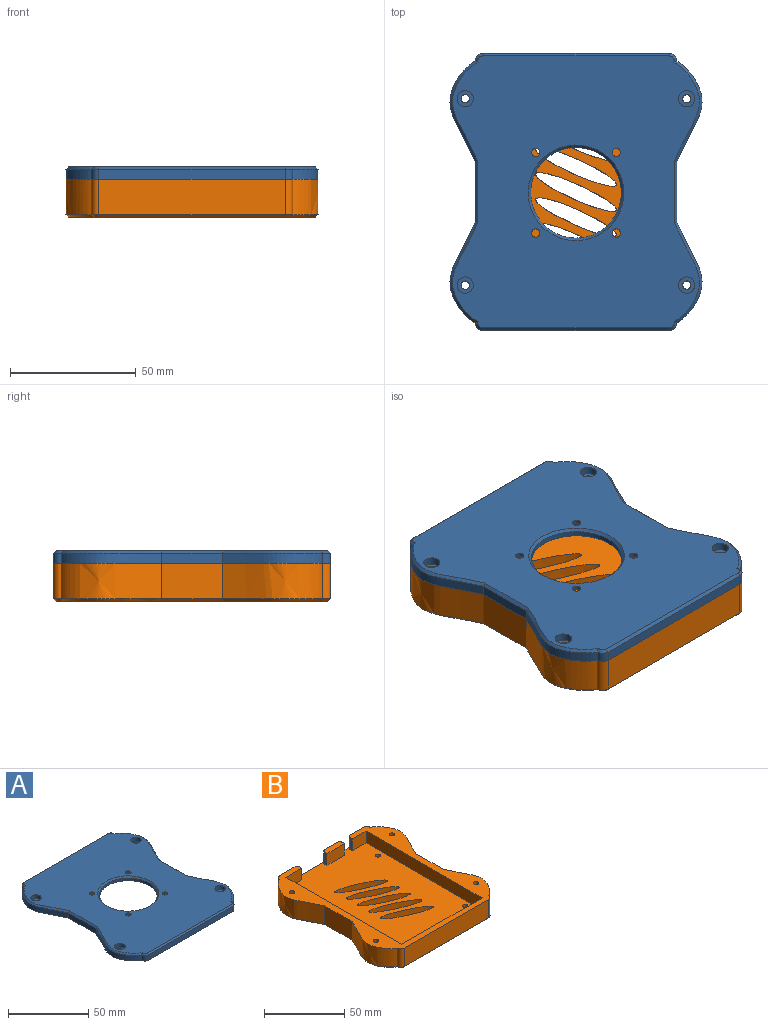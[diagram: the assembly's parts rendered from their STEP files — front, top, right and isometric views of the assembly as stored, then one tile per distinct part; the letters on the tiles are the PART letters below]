
ASSEMBLY  parts=2 mates=1
PART A: 53 faces, bbox 102.5x111.1x6.1 mm
  f0: plane 70.5x2mm, normal (0,1,0), area 141mm2, adj f1,f15,f16,f30
  f1: plane 102x2mm, normal (1,0,0), area 204mm2, adj f0,f2,f16,f30
  f2: plane 70.5x2mm, normal (0,-1,0), area 141mm2, adj f1,f15,f16,f30
  f3: extruded ~40x10.04mm, area 183.4mm2, adj f4,f14,f16,f51
  f4: plane 24x4mm, normal (-1,0,0), area 96mm2, adj f3,f5,f16,f49
  f5: extruded ~40x10.04mm, area 183.4mm2, adj f4,f6,f16,f47
  f6: cylinder r=3mm len=4mm, axis (0,0,1), area 18.8mm2, adj f5,f7,f16,f45
  f7: plane 74x4mm, normal (0,-1,0), area 296mm2, adj f6,f8,f16,f43
  f8: cylinder r=3mm len=4mm, axis (0,0,1), area 18.8mm2, adj f7,f9,f16,f41
  f9: extruded ~40x10.04mm, area 183.4mm2, adj f8,f10,f16,f42
  f10: plane 24x4mm, normal (1,0,0), area 96mm2, adj f9,f11,f16,f44
  f11: extruded ~40x10.04mm, area 183.4mm2, adj f10,f12,f16,f46
  f12: cylinder r=3mm len=4mm, axis (0,0,1), area 18.8mm2, adj f11,f13,f16,f48
  f13: plane 74x4mm, normal (0,1,0), area 296mm2, adj f12,f14,f16,f50
  f14: cylinder r=3mm len=4mm, axis (0,0,1), area 18.8mm2, adj f3,f13,f16,f52
  f15: plane 102x2mm, normal (-1,0,0), area 204mm2, adj f0,f2,f16,f30
  f16: plane 110x101.38mm, normal (0,0,-1), area 2552.6mm2, adj f0,f1,f2,f3,f4,f5,f6,f7
  f17: plane 109.12x99.61mm, normal (0,0,1), area 8092.7mm2, adj f20,f23,f26,f29,f31,f33,f35,f37
  f18: cylinder r=1.65mm len=3.3mm, axis (0,0,1), area 20.7mm2, adj f16,f19
  f19: plane 6.5x6.5mm, normal (0,0,1), area 24.6mm2, adj f18,f20
  f20: cylinder r=3.25mm len=6.5mm, axis (0,0,1), area 61.3mm2, adj f17,f19
  f21: cylinder r=1.65mm len=3.3mm, axis (0,0,1), area 20.7mm2, adj f16,f22
  f22: plane 6.5x6.5mm, normal (0,0,1), area 24.6mm2, adj f21,f23
  f23: cylinder r=3.25mm len=6.5mm, axis (0,0,1), area 61.3mm2, adj f17,f22
  f24: cylinder r=1.65mm len=3.3mm, axis (0,0,1), area 20.7mm2, adj f16,f25
  f25: plane 6.5x6.5mm, normal (0,0,1), area 24.6mm2, adj f24,f26
  f26: cylinder r=3.25mm len=6.5mm, axis (0,0,1), area 61.3mm2, adj f17,f25
  f27: cylinder r=1.65mm len=3.3mm, axis (0,0,1), area 20.7mm2, adj f16,f28
  f28: plane 6.5x6.5mm, normal (0,0,1), area 24.6mm2, adj f27,f29
  f29: cylinder r=3.25mm len=6.5mm, axis (0,0,1), area 61.3mm2, adj f17,f28
  f30: plane 102x70.5mm, normal (0,0,-1), area 6031.3mm2, adj f0,f1,f2,f15,f32,f34,f36,f38
  f31: cylinder r=1.65mm len=3.3mm, axis (0,0,-1), area 13.4mm2, adj f17,f32
  f32: cone r=1.65mm half-angle=45deg, axis (0,0,-1), area 38.1mm2, adj f30,f31
  f33: cylinder r=1.65mm len=3.3mm, axis (0,0,-1), area 13.4mm2, adj f17,f34
  f34: cone r=1.65mm half-angle=45deg, axis (0,0,-1), area 38.1mm2, adj f30,f33
  f35: cylinder r=1.65mm len=3.3mm, axis (0,0,-1), area 13.4mm2, adj f17,f36
  f36: cone r=1.65mm half-angle=45deg, axis (0,0,-1), area 38.1mm2, adj f30,f35
  f37: cylinder r=1.65mm len=3.3mm, axis (0,0,-1), area 13.4mm2, adj f17,f38
  f38: cone r=1.65mm half-angle=45deg, axis (0,0,-1), area 38.1mm2, adj f30,f37
  f39: cylinder r=18mm len=36mm, axis (0,0,-1), area 226.2mm2, adj f30,f40
  f40: cone r=18mm half-angle=45deg, axis (0,0,1), area 164.4mm2, adj f17,f39
  f41: cone r=2mm half-angle=45deg, axis (0,0,-1), area 6mm2, adj f8,f17,f42,f43
  f42: bspline ~40.52x11.13mm, area 64.4mm2, adj f9,f17,f41,f44
  f43: plane 74x1mm, normal (0,-0.71,0.71), area 104.7mm2, adj f7,f17,f41,f45
  f44: plane 24.39x1mm, normal (0.71,0,0.71), area 34.2mm2, adj f10,f17,f42,f46
  f45: cone r=2mm half-angle=45deg, axis (0,0,-1), area 6mm2, adj f6,f17,f43,f47
  f46: bspline ~43.19x12.21mm, area 64.4mm2, adj f11,f17,f44,f48
  f47: bspline ~43.19x12.21mm, area 64.4mm2, adj f5,f17,f45,f49
  f48: cone r=2mm half-angle=45deg, axis (0,0,-1), area 6mm2, adj f12,f17,f46,f50
  f49: plane 24.39x1mm, normal (-0.71,0,0.71), area 34.2mm2, adj f4,f17,f47,f51
  f50: plane 74x1mm, normal (0,0.71,0.71), area 104.7mm2, adj f13,f17,f48,f52
  f51: bspline ~40.52x11.13mm, area 64.4mm2, adj f3,f17,f49,f52
  f52: cone r=2mm half-angle=45deg, axis (0,0,-1), area 6mm2, adj f14,f17,f50,f51
PART B: 96 faces, bbox 102.5x111.1x16.1 mm
  f0: plane 15.5x9mm, normal (0,-1,0), area 139.5mm2, adj f2,f21,f67,f68
  f1: plane 12x9mm, normal (0,-1,0), area 108mm2, adj f3,f8,f21,f66
  f2: plane 15.5x4mm, normal (0,0,1), area 60.3mm2, adj f0,f4,f67,f68,f71,f73
  f3: plane 110x101.38mm, normal (0,0,1), area 2372.9mm2, adj f1,f4,f6,f7,f8,f9,f10,f11
  f4: plane 74x14mm, normal (0,1,0), area 703mm2, adj f2,f3,f12,f13,f21,f70,f71,f72
  f5: plane 109.12x99.61mm, normal (0,0,-1), area 7932mm2, adj f24,f27,f30,f33,f38,f39,f40,f41
  f6: plane 102x9mm, normal (1,0,0), area 918mm2, adj f3,f7,f9,f21
  f7: plane 70.5x9mm, normal (0,1,0), area 634.5mm2, adj f3,f6,f8,f21
  f8: plane 102x9mm, normal (-1,0,0), area 918mm2, adj f1,f3,f7,f21
  f9: plane 14x9mm, normal (0,-1,0), area 126mm2, adj f3,f6,f21,f69
  f10: plane 24x14mm, normal (1,0,0), area 336mm2, adj f3,f11,f20,f83
  f11: extruded ~40x14mm, area 641.9mm2, adj f3,f10,f12,f81
  f12: cylinder r=3mm len=14mm, axis (0,0,-1), area 66mm2, adj f3,f4,f11,f79
  f13: cylinder r=3mm len=14mm, axis (0,0,-1), area 66mm2, adj f3,f4,f14,f82
  f14: extruded ~40x14mm, area 641.9mm2, adj f3,f13,f15,f84
  f15: plane 24x14mm, normal (-1,0,0), area 336mm2, adj f3,f14,f16,f86
  f16: extruded ~40x14mm, area 641.9mm2, adj f3,f15,f17,f88
  f17: cylinder r=3mm len=14mm, axis (0,0,-1), area 66mm2, adj f3,f16,f18,f90
  f18: plane 74x14mm, normal (0,-1,0), area 1036mm2, adj f3,f17,f19,f89
  f19: cylinder r=3mm len=14mm, axis (0,0,-1), area 66mm2, adj f3,f18,f20,f87
  f20: extruded ~40x14mm, area 641.9mm2, adj f3,f10,f19,f85
  f21: plane 106x70.5mm, normal (0,0,1), area 6451.6mm2, adj f0,f1,f4,f6,f7,f8,f9,f22
  f22: cylinder r=1.65mm len=3.3mm, axis (0,0,-1), area 31.1mm2, adj f21,f23
  f23: plane 6.5x6.5mm, normal (0,0,-1), area 24.6mm2, adj f22,f24
  f24: cylinder r=3.25mm len=6.5mm, axis (0,0,-1), area 61.3mm2, adj f5,f23
  f25: cylinder r=1.65mm len=3.3mm, axis (0,0,-1), area 31.1mm2, adj f21,f26
  f26: plane 6.5x6.5mm, normal (0,0,-1), area 24.6mm2, adj f25,f27
  f27: cylinder r=3.25mm len=6.5mm, axis (0,0,-1), area 61.3mm2, adj f5,f26
  f28: cylinder r=1.65mm len=3.3mm, axis (0,0,-1), area 31.1mm2, adj f21,f29
  f29: plane 6.5x6.5mm, normal (0,0,-1), area 24.6mm2, adj f28,f30
  f30: cylinder r=3.25mm len=6.5mm, axis (0,0,-1), area 61.3mm2, adj f5,f29
  f31: cylinder r=1.65mm len=3.3mm, axis (0,0,-1), area 31.1mm2, adj f21,f32
  f32: plane 6.5x6.5mm, normal (0,0,-1), area 24.6mm2, adj f31,f33
  f33: cylinder r=3.25mm len=6.5mm, axis (0,0,-1), area 61.3mm2, adj f5,f32
  f34: cylinder r=1.65mm len=13mm, axis (0,0,-1), area 134.8mm2, adj f3,f65
  f35: cylinder r=1.65mm len=13mm, axis (0,0,-1), area 134.8mm2, adj f3,f58
  f36: cylinder r=1.65mm len=13mm, axis (0,0,-1), area 134.8mm2, adj f3,f51
  f37: cylinder r=1.65mm len=13mm, axis (0,0,-1), area 134.8mm2, adj f3,f44
  f38: plane 3.46x2mm, normal (-1,0,0), area 6.9mm2, adj f5,f39,f43,f44
  f39: plane 3x2mm, normal (-0.5,-0.87,0), area 6.9mm2, adj f5,f38,f40,f44
  f40: plane 3x2mm, normal (0.5,-0.87,0), area 6.9mm2, adj f5,f39,f41,f44
  f41: plane 3.46x2mm, normal (1,0,0), area 6.9mm2, adj f5,f40,f42,f44
  f42: plane 3x2mm, normal (0.5,0.87,0), area 6.9mm2, adj f5,f41,f43,f44
  f43: plane 3x2mm, normal (-0.5,0.87,0), area 6.9mm2, adj f5,f38,f42,f44
  f44: plane 6.93x6mm, normal (0,0,-1), area 22.6mm2, adj f37,f38,f39,f40,f41,f42,f43
  f45: plane 3x2mm, normal (-0.5,-0.87,0), area 6.9mm2, adj f5,f46,f50,f51
  f46: plane 3x2mm, normal (0.5,-0.87,0), area 6.9mm2, adj f5,f45,f47,f51
  f47: plane 3.46x2mm, normal (1,0,0), area 6.9mm2, adj f5,f46,f48,f51
  f48: plane 3x2mm, normal (0.5,0.87,0), area 6.9mm2, adj f5,f47,f49,f51
  f49: plane 3x2mm, normal (-0.5,0.87,0), area 6.9mm2, adj f5,f48,f50,f51
  f50: plane 3.46x2mm, normal (-1,0,0), area 6.9mm2, adj f5,f45,f49,f51
  f51: plane 6.93x6mm, normal (0,0,-1), area 22.6mm2, adj f36,f45,f46,f47,f48,f49,f50
  f52: plane 3.46x2mm, normal (-1,0,0), area 6.9mm2, adj f5,f53,f57,f58
  f53: plane 3x2mm, normal (-0.5,-0.87,0), area 6.9mm2, adj f5,f52,f54,f58
  f54: plane 3x2mm, normal (0.5,-0.87,0), area 6.9mm2, adj f5,f53,f55,f58
  f55: plane 3.46x2mm, normal (1,0,0), area 6.9mm2, adj f5,f54,f56,f58
  f56: plane 3x2mm, normal (0.5,0.87,0), area 6.9mm2, adj f5,f55,f57,f58
  f57: plane 3x2mm, normal (-0.5,0.87,0), area 6.9mm2, adj f5,f52,f56,f58
  f58: plane 6.93x6mm, normal (0,0,-1), area 22.6mm2, adj f35,f52,f53,f54,f55,f56,f57
  f59: plane 3x2mm, normal (0.5,0.87,0), area 6.9mm2, adj f5,f60,f64,f65
  f60: plane 3x2mm, normal (-0.5,0.87,0), area 6.9mm2, adj f5,f59,f61,f65
  f61: plane 3.46x2mm, normal (-1,0,0), area 6.9mm2, adj f5,f60,f62,f65
  f62: plane 3x2mm, normal (-0.5,-0.87,0), area 6.9mm2, adj f5,f61,f63,f65
  f63: plane 3x2mm, normal (0.5,-0.87,0), area 6.9mm2, adj f5,f62,f64,f65
  f64: plane 3.46x2mm, normal (1,0,0), area 6.9mm2, adj f5,f59,f63,f65
  f65: plane 6.93x6mm, normal (0,0,-1), area 22.6mm2, adj f34,f59,f60,f61,f62,f63,f64
  f66: plane 9x2mm, normal (-1,0,0), area 18mm2, adj f1,f3,f21,f70
  f67: plane 9x2mm, normal (1,0,0), area 18mm2, adj f0,f2,f21,f71
  f68: plane 9x2mm, normal (-1,0,0), area 18mm2, adj f0,f2,f21,f73
  f69: plane 9x2mm, normal (1,0,0), area 18mm2, adj f3,f9,f21,f72
  f70: cylinder r=2mm len=9mm, axis (0,0,1), area 28.3mm2, adj f3,f4,f21,f66
  f71: cylinder r=2mm len=9mm, axis (0,0,-1), area 28.3mm2, adj f2,f4,f21,f67
  f72: cylinder r=2mm len=9mm, axis (0,0,-1), area 28.3mm2, adj f3,f4,f21,f69
  f73: cylinder r=2mm len=9mm, axis (0,0,1), area 28.3mm2, adj f2,f4,f21,f68
  f74: extruded ~31.9x15.39mm, area 364.4mm2, adj f21,f95
  f75: extruded ~31.9x15.39mm, area 364.4mm2, adj f21,f92
  f76: extruded ~31.9x15.39mm, area 364.4mm2, adj f21,f91
  f77: extruded ~31.9x15.39mm, area 364.4mm2, adj f21,f94
  f78: extruded ~31.9x15.39mm, area 364.4mm2, adj f21,f93
  f79: cone r=3mm half-angle=45deg, axis (0,0,1), area 6mm2, adj f5,f12,f80,f81
  f80: plane 74x1mm, normal (0,0.71,-0.71), area 104.7mm2, adj f4,f5,f79,f82
  f81: bspline ~40.52x11.13mm, area 64.4mm2, adj f5,f11,f79,f83
  f82: cone r=3mm half-angle=45deg, axis (0,0,1), area 6mm2, adj f5,f13,f80,f84
  f83: plane 24.39x1mm, normal (0.71,0,-0.71), area 34.2mm2, adj f5,f10,f81,f85
  f84: bspline ~43.17x12.24mm, area 64.4mm2, adj f5,f14,f82,f86
  f85: bspline ~43.17x12.24mm, area 64.4mm2, adj f5,f20,f83,f87
  f86: plane 24.39x1mm, normal (-0.71,0,-0.71), area 34.2mm2, adj f5,f15,f84,f88
  f87: cone r=3mm half-angle=45deg, axis (0,0,1), area 6mm2, adj f5,f19,f85,f89
  f88: bspline ~40.52x11.13mm, area 64.4mm2, adj f5,f16,f86,f90
  f89: plane 74x1mm, normal (0,-0.71,-0.71), area 104.7mm2, adj f5,f18,f87,f90
  f90: cone r=3mm half-angle=45deg, axis (0,0,1), area 6mm2, adj f5,f17,f88,f89
  f91: bspline ~34x17.41mm, area 117.9mm2, adj f5,f76
  f92: bspline ~34x17.41mm, area 117.9mm2, adj f5,f75
  f93: bspline ~34x17.41mm, area 117.9mm2, adj f5,f78
  f94: bspline ~34x17.41mm, area 117.9mm2, adj f5,f77
  f95: bspline ~34x17.41mm, area 117.9mm2, adj f5,f74
PLACE A t=(72.53,-16.36,30.91)mm
PLACE B t=(72.53,-16.03,10.91)mm
MATE fastened B.f36 <-> A.f24  axis (0,0,1) through (116.53,-53.03,25.91)mm
